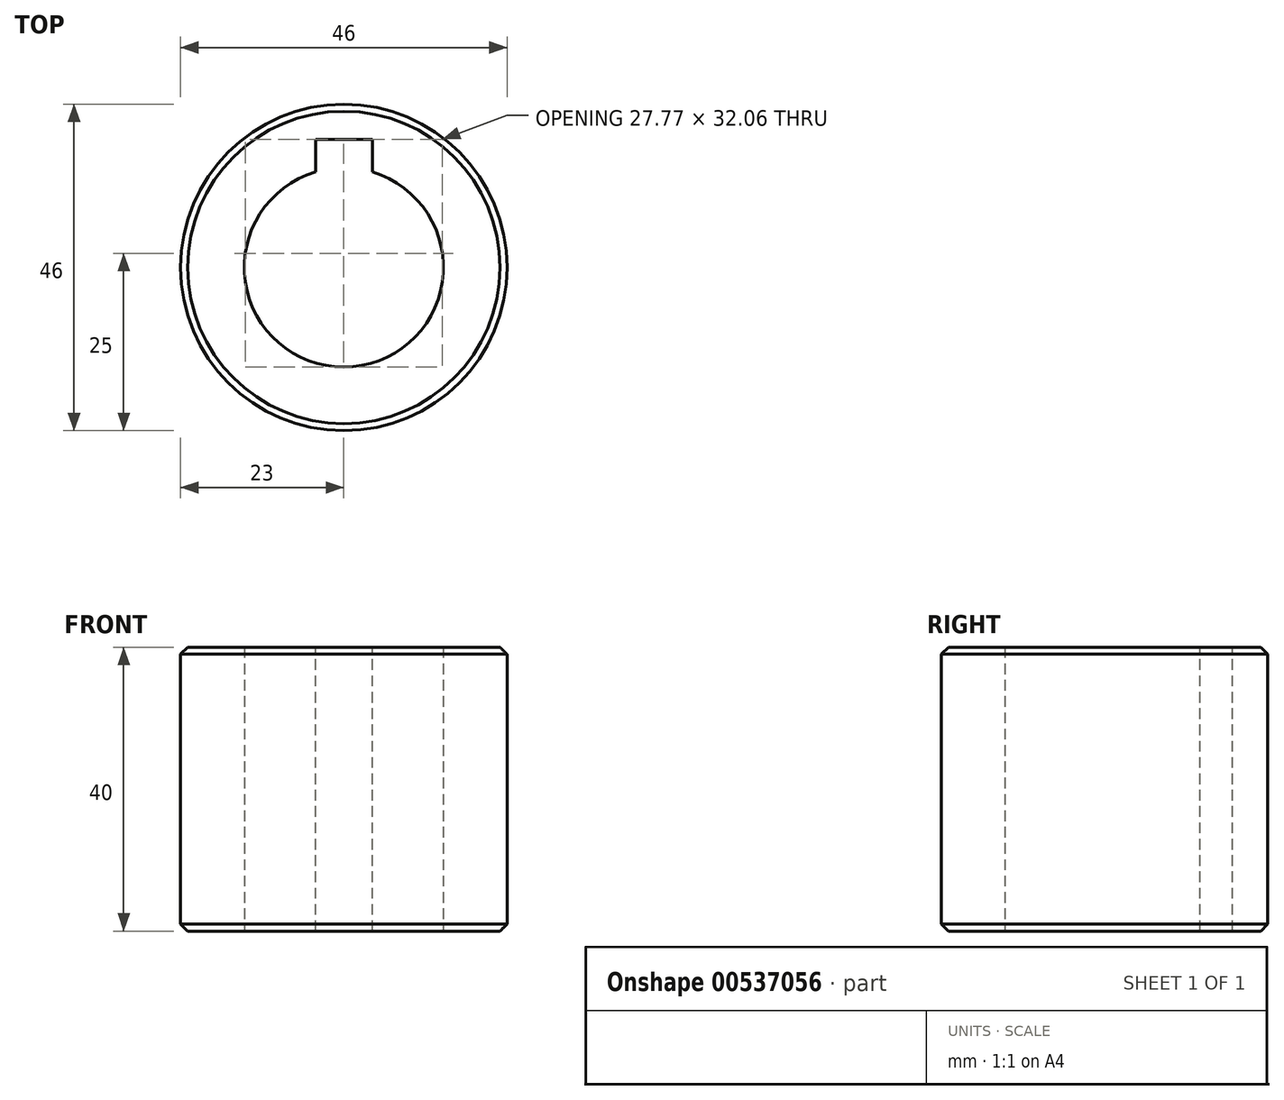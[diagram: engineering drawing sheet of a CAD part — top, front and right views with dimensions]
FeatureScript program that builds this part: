
annotation { "Feature Type Name" : "Feature", "Feature Type Description" : "" }
export const myFeature = defineFeature(function(context is Context, id is Id, definition is map)
    precondition{}
    {
        {
            var Q0;
            Q0=qCreatedBy(makeId("Top.planeOp"),FACE);
            var sketch = newSketch(context, id + "F0", { "sketchPlane" : qUnion([Q0])});
            skCircle(sketch, "E0", {"center": v(0, 0) * mm, "radius": 23 * mm});
            skCircle(sketch, "E1", {"center": v(0, 0) * mm, "radius": 14.03 * mm});
            skSolve(sketch);
        }
        {
            var Q0;
            Q0=makeQuery(id+"F0.imprint","IMPRINT",FACE,{"disambiguationData":[TD([[makeQuery(id+"F0.imprint","IMPRINT",EDGE,{"derivedFrom":sQuery(id+"F0.wireOp",EDGE,"E0")}),1.0]])]});
            extrude(context, id + "F1", {"entities" : qUnion([Q0]), "depth" : 40 * mm, "offsetDistance" : 25 * mm});
        }
        {
            var Q0;
            Q0=makeQuery(id+"F1.opExtrude","CAP_FACE",FACE,{"disambiguationData":[OSD([sQuery(id+"F0.wireOp",EDGE,"E0"),sQuery(id+"F0.wireOp",EDGE,"E1")])],"isStart":false});
            var sketch = newSketch(context, id + "F2", { "sketchPlane" : qUnion([Q0])});
            skLineSegment(sketch, "E2.bottom", {"start": v(4, 18.03) * mm, "end": v(-4, 18.03) * mm});
            skLineSegment(sketch, "E2.top", {"start": v(4, 10.03) * mm, "end": v(-4, 10.03) * mm});
            skLineSegment(sketch, "E2.left", {"start": v(4, 18.03) * mm, "end": v(4, 10.03) * mm});
            skLineSegment(sketch, "E2.right", {"start": v(-4, 18.03) * mm, "end": v(-4, 10.03) * mm});
            skPoint(sketch, "E2.middle", {"position": v(0, 14.03) * mm});
            skSolve(sketch);
        }
        {
            var Q0;
            {var subQ0=sQuery(id+"F2.wireOp",EDGE,"E2.bottom");Q0=makeQuery(id+"F2.imprint","IMPRINT",FACE,{"disambiguationData":[TD([[makeQuery(id+"F2.imprint","IMPRINT",EDGE,{"derivedFrom":subQ0}),1.0]])]});}
            extrude(context, id + "F3", {"entities" : qUnion([Q0]), "operationType" : NewBodyOperationType.REMOVE, "endBound" : BoundingType.THROUGH_ALL, "oppositeDirection" : true, "depth" : 25 * mm, "offsetDistance" : 25 * mm});
        }
        {
            var Q0;
            Q0=makeQuery(id+"F1.opExtrude","CAP_EDGE",EDGE,{"disambiguationData":[OSD([sQuery(id+"F0.wireOp",EDGE,"E0")])],"isStart":false});
            var Q1;
            Q1=makeQuery(id+"F1.opExtrude","CAP_EDGE",EDGE,{"disambiguationData":[OSD([sQuery(id+"F0.wireOp",EDGE,"E0")])],"isStart":true});
            chamfer(context, id + "F4", {"entities" : qUnion([Q0, Q1]), "width" : 1 * mm, "tangentPropagation" : true});
        }
    });
